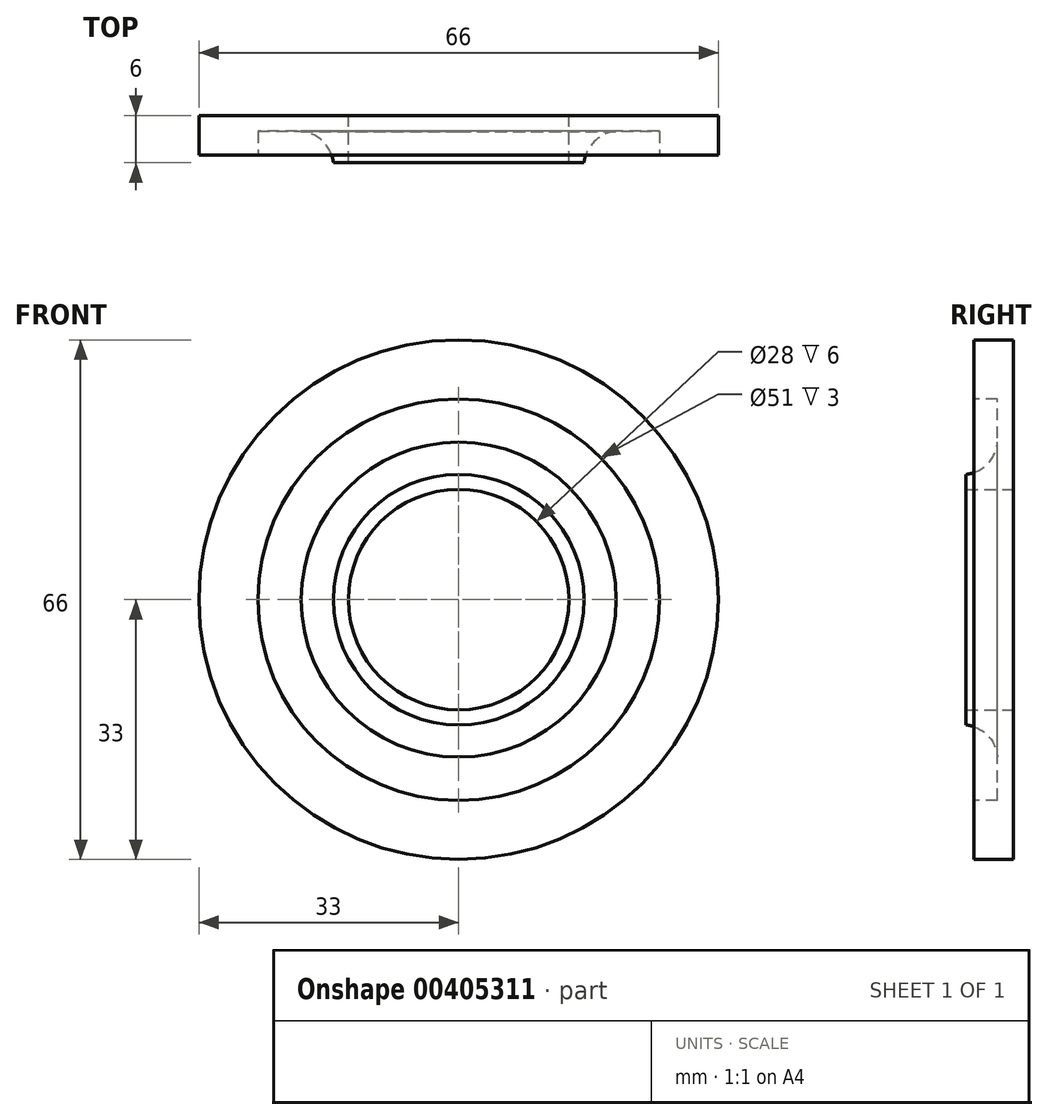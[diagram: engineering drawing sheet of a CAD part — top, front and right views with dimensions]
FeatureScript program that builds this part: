
annotation { "Feature Type Name" : "Feature", "Feature Type Description" : "" }
export const myFeature = defineFeature(function(context is Context, id is Id, definition is map)
    precondition{}
    {
        {
            var Q0;
            Q0=qCreatedBy(makeId("Front.planeOp"),FACE);
            var sketch = newSketch(context, id + "F0", { "sketchPlane" : qUnion([Q0])});
            skCircle(sketch, "E0", {"center": v(0, 0) * mm, "radius": 14 * mm});
            skCircle(sketch, "E1", {"center": v(0, 0) * mm, "radius": 33 * mm});
            skSolve(sketch);
        }
        {
            var Q0;
            Q0 = qSketchRegion(id + "F0", true);
            extrude(context, id + "F1", {"entities" : qUnion([Q0]), "depth" : 5 * mm, "offsetDistance" : 25 * mm});
        }
        {
            var Q0;
            Q0=makeQuery(id+"F1.opExtrude","CAP_FACE",FACE,{"disambiguationData":[OSD([sQuery(id+"F0.wireOp",EDGE,"E0"),sQuery(id+"F0.wireOp",EDGE,"E1")])],"isStart":false});
            var sketch = newSketch(context, id + "F2", { "sketchPlane" : qUnion([Q0])});
            skCircle(sketch, "E2", {"center": v(0, 0) * mm, "radius": 14 * mm});
            skCircle(sketch, "E3", {"center": v(0, 0) * mm, "radius": 25.5 * mm});
            skSolve(sketch);
        }
        {
            var Q0;
            Q0 = qSketchRegion(id + "F2", true);
            extrude(context, id + "F3", {"entities" : qUnion([Q0]), "operationType" : NewBodyOperationType.REMOVE, "oppositeDirection" : true, "depth" : 3 * mm});
        }
        {
            var Q0;
            Q0=makeQuery(id+"F3.boolean.opBoolean","COPY",FACE,{"derivedFrom":makeQuery(id+"F3.opExtrude","CAP_FACE",FACE,{"disambiguationData":[OSD([sQuery(id+"F2.wireOp",EDGE,"E2"),sQuery(id+"F2.wireOp",EDGE,"E3")])],"isStart":false})});
            var sketch = newSketch(context, id + "F4", { "sketchPlane" : qUnion([Q0])});
            skCircle(sketch, "E4", {"center": v(0, 0) * mm, "radius": 14 * mm});
            skCircle(sketch, "E5", {"center": v(0, 0) * mm, "radius": 20 * mm});
            skSolve(sketch);
        }
        {
            var Q0;
            Q0=makeQuery(id+"F4.imprint","IMPRINT",FACE,{"disambiguationData":[TD([[makeQuery(id+"F4.imprint","IMPRINT",EDGE,{"derivedFrom":sQuery(id+"F4.wireOp",EDGE,"E4")}),-1.0]])]});
            extrude(context, id + "F5", {"entities" : qUnion([Q0]), "operationType" : NewBodyOperationType.ADD, "depth" : 4 * mm});
        }
        {
            var Q0;
            Q0=qCreatedBy(makeId("Top.planeOp"),FACE);
            var sketch = newSketch(context, id + "F6", { "sketchPlane" : qUnion([Q0])});
            skCircle(sketch, "E6", {"center": v(20.39, -6.5) * mm, "radius": 4.5 * mm});
            skLineSegment(sketch, "E7", {"start": v(20.39, -6.5) * mm, "end": v(25.49, -6.5) * mm});
            skLineSegment(sketch, "E8", {"start": v(20.39, -2) * mm, "end": v(20.39, 0) * mm});
            skSolve(sketch);
        }
        {
            var Q0;
            {var subQ0=sQuery(id+"F6.wireOp",EDGE,"E6");Q0=makeQuery(id+"F6.imprint","IMPRINT",FACE,{"disambiguationData":[TD([[makeQuery(id+"F6.imprint","IMPRINT",EDGE,{"disambiguationData":[TD([[makeQuery(id+"F6.imprint","IMPRINT",VERTEX,{"derivedFrom":subQ0}),-1.0]])],"derivedFrom":subQ0}),1.0]])]});}
            var Q1;
            Q1=makeQuery(id+"F5.opExtrude","CAP_EDGE",EDGE,{"disambiguationData":[OSD([sQuery(id+"F4.wireOp",EDGE,"E5")])],"isStart":false});
            revolve(context, id + "F7", {"operationType" : NewBodyOperationType.REMOVE, "entities" : qUnion([Q0]), "axis" : qUnion([Q1]), "revolveType" : RevolveType.FULL, "oppositeDirection" : true});
        }
    });
